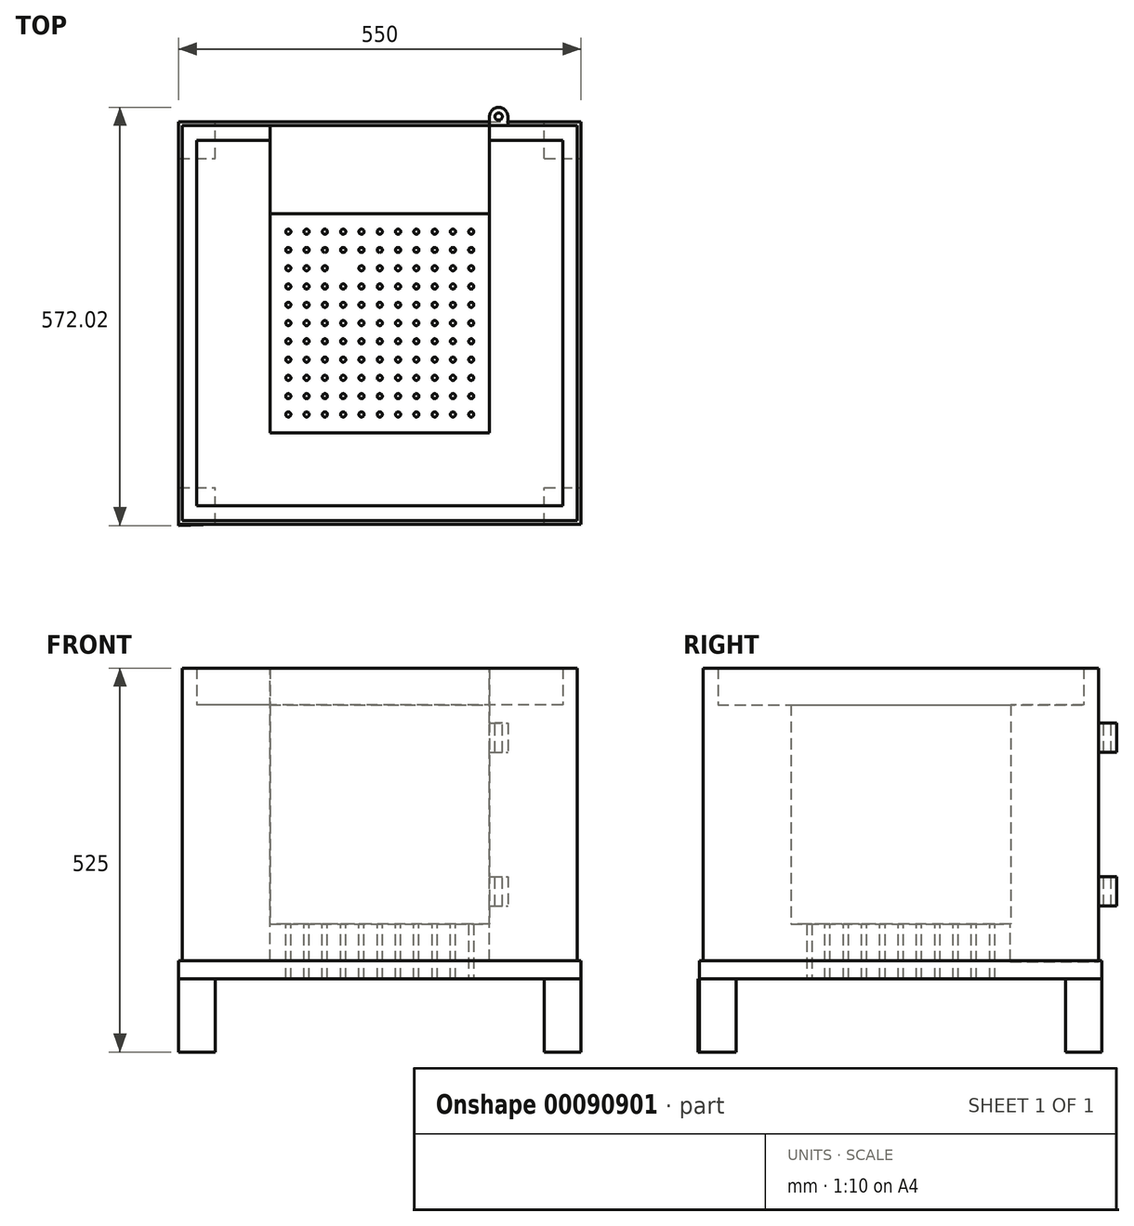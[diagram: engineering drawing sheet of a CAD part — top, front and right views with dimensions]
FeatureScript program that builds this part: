
annotation { "Feature Type Name" : "Feature", "Feature Type Description" : "" }
export const myFeature = defineFeature(function(context is Context, id is Id, definition is map)
    precondition{}
    {
        {
            var Q0;
            Q0=qCreatedBy(makeId("Top.planeOp"),FACE);
            var sketch = newSketch(context, id + "F0", { "sketchPlane" : qUnion([Q0])});
            skPoint(sketch, "E0.middle", {"position": v(0, 0) * mm});
            skLineSegment(sketch, "E1.bottom", {"start": v(225, 225) * mm, "end": v(275, 225) * mm});
            skLineSegment(sketch, "E1.top", {"start": v(225, 275) * mm, "end": v(275, 275) * mm});
            skLineSegment(sketch, "E1.left", {"start": v(225, 225) * mm, "end": v(225, 275) * mm});
            skLineSegment(sketch, "E1.right", {"start": v(275, 225) * mm, "end": v(275, 275) * mm});
            skLineSegment(sketch, "E2.top", {"start": v(225, -225) * mm, "end": v(275, -225) * mm});
            skLineSegment(sketch, "E2.left", {"start": v(225, -275) * mm, "end": v(225, -225) * mm});
            skLineSegment(sketch, "E2.right", {"start": v(275, -275) * mm, "end": v(275, -225) * mm});
            skLineSegment(sketch, "E3", {"start": v(225, -275) * mm, "end": v(275, -275) * mm});
            skLineSegment(sketch, "E4.top", {"start": v(-275, -225) * mm, "end": v(-225, -225) * mm});
            skLineSegment(sketch, "E4.left", {"start": v(-275, -277.02) * mm, "end": v(-275, -225) * mm});
            skLineSegment(sketch, "E4.right", {"start": v(-225, -275) * mm, "end": v(-225, -225) * mm});
            skLineSegment(sketch, "E5", {"start": v(-275, -277.02) * mm, "end": v(-225, -275) * mm});
            skLineSegment(sketch, "E6.top", {"start": v(-275, 275) * mm, "end": v(-225, 275) * mm});
            skLineSegment(sketch, "E6.left", {"start": v(-275, 225) * mm, "end": v(-275, 275) * mm});
            skLineSegment(sketch, "E6.right", {"start": v(-225, 225) * mm, "end": v(-225, 275) * mm});
            skLineSegment(sketch, "E7", {"start": v(-275, 225) * mm, "end": v(-225, 225) * mm});
            skSolve(sketch);
        }
        {
            var Q0;
            Q0=makeQuery(id+"F0.imprint","IMPRINT",FACE,{"disambiguationData":[TD([[makeQuery(id+"F0.imprint","IMPRINT",EDGE,{"derivedFrom":sQuery(id+"F0.wireOp",EDGE,"E1.bottom")}),1.0]])]});
            var Q1;
            Q1=makeQuery(id+"F0.imprint","IMPRINT",FACE,{"disambiguationData":[TD([[makeQuery(id+"F0.imprint","IMPRINT",EDGE,{"derivedFrom":sQuery(id+"F0.wireOp",EDGE,"E2.top")}),-1.0]])]});
            var Q2;
            Q2=makeQuery(id+"F0.imprint","IMPRINT",FACE,{"disambiguationData":[TD([[makeQuery(id+"F0.imprint","IMPRINT",EDGE,{"derivedFrom":sQuery(id+"F0.wireOp",EDGE,"E4.top")}),-1.0]])]});
            var Q3;
            Q3=makeQuery(id+"F0.imprint","IMPRINT",FACE,{"disambiguationData":[TD([[makeQuery(id+"F0.imprint","IMPRINT",EDGE,{"derivedFrom":sQuery(id+"F0.wireOp",EDGE,"E6.top")}),-1.0]])]});
            extrude(context, id + "F1", {"entities" : qUnion([Q0, Q1, Q2, Q3]), "depth" : 100 * mm});
        }
        {
            var Q0;
            Q0=makeQuery(id+"F1.opExtrude","CAP_FACE",FACE,{"disambiguationData":[OSD([sQuery(id+"F0.wireOp",EDGE,"E6.top"),sQuery(id+"F0.wireOp",EDGE,"E6.left"),sQuery(id+"F0.wireOp",EDGE,"E6.right"),sQuery(id+"F0.wireOp",EDGE,"E7")])],"isStart":false});
            var sketch = newSketch(context, id + "F2", { "sketchPlane" : qUnion([Q0])});
            skLineSegment(sketch, "E8.bottom", {"start": v(-275, 275) * mm, "end": v(275, 275) * mm});
            skLineSegment(sketch, "E8.top", {"start": v(-275, -275) * mm, "end": v(275, -275) * mm});
            skLineSegment(sketch, "E8.left", {"start": v(-275, 275) * mm, "end": v(-275, -275) * mm});
            skLineSegment(sketch, "E8.right", {"start": v(275, 275) * mm, "end": v(275, -275) * mm});
            skSolve(sketch);
        }
        {
            var Q0;
            Q0 = qSketchRegion(id + "F2", true);
            var Q1;
            {var subQ3=sQuery(id+"F2.wireOp",EDGE,"E8.top");Q1=makeQuery(id+"F2.imprint","IMPRINT",FACE,{"disambiguationData":[TD([[makeQuery(id+"F2.imprint","IMPRINT",EDGE,{"derivedFrom":subQ3}),1.0]])]});}
            extrude(context, id + "F3", {"entities" : qUnion([Q0, Q1]), "depth" : 25 * mm});
        }
        {
            var Q0;
            Q0=makeQuery(id+"F3.opExtrude","CAP_FACE",FACE,{"disambiguationData":[OSD([sQuery(id+"F2.wireOp",EDGE,"E8.bottom"),sQuery(id+"F2.wireOp",EDGE,"E8.top"),sQuery(id+"F2.wireOp",EDGE,"E8.left"),sQuery(id+"F2.wireOp",EDGE,"E8.right")])],"isStart":false});
            var sketch = newSketch(context, id + "F4", { "sketchPlane" : qUnion([Q0])});
            skLineSegment(sketch, "E9.bottom", {"start": v(250, -250) * mm, "end": v(-250, -250) * mm});
            skLineSegment(sketch, "E9.top", {"start": v(250, 250) * mm, "end": v(-250, 250) * mm});
            skLineSegment(sketch, "E9.left", {"start": v(250, -250) * mm, "end": v(250, 250) * mm});
            skLineSegment(sketch, "E9.right", {"start": v(-250, -250) * mm, "end": v(-250, 250) * mm});
            skLineSegment(sketch, "E10.0", {"start": v(150, 150) * mm, "end": v(-150, 150) * mm});
            skLineSegment(sketch, "E10.1", {"start": v(150, -150) * mm, "end": v(150, 150) * mm});
            skLineSegment(sketch, "E10.2", {"start": v(-150, -150) * mm, "end": v(150, -150) * mm});
            skLineSegment(sketch, "E10.3", {"start": v(-150, 150) * mm, "end": v(-150, -150) * mm});
            skLineSegment(sketch, "E11.0", {"start": v(270, 270) * mm, "end": v(-270, 270) * mm});
            skLineSegment(sketch, "E11.1", {"start": v(270, -270) * mm, "end": v(270, 270) * mm});
            skLineSegment(sketch, "E11.2", {"start": v(-270, -270) * mm, "end": v(270, -270) * mm});
            skLineSegment(sketch, "E11.3", {"start": v(-270, 270) * mm, "end": v(-270, -270) * mm});
            skLineSegment(sketch, "E12", {"start": v(-150, 150) * mm, "end": v(-150, 275) * mm});
            skLineSegment(sketch, "E13", {"start": v(150, 150) * mm, "end": v(150, 275) * mm});
            skLineSegment(sketch, "E14.direction2", {"start": v(125, -125) * mm, "end": v(125, -104.2) * mm, "construction": true});
            skCircle(sketch, "E15", {"center": v(125, -125) * mm, "radius": 3.5 * mm});
            skSolve(sketch);
        }
        {
            var Q0;
            Q0=makeQuery(id+"F4.imprint","IMPRINT",FACE,{"disambiguationData":[TD([[makeQuery(id+"F4.imprint","IMPRINT",EDGE,{"derivedFrom":sQuery(id+"F4.wireOp",EDGE,"E9.bottom")}),1.0]])]});
            var Q1;
            {var subQ0=sQuery(id+"F4.wireOp",EDGE,"E13");var subQ1=sQuery(id+"F4.wireOp",EDGE,"E9.top");var subQ2=makeQuery(id+"F4.imprint","INTERSECT",VERTEX,{"derivedFrom":[subQ1,subQ0]});Q1=makeQuery(id+"F4.imprint","IMPRINT",FACE,{"disambiguationData":[TD([[makeQuery(id+"F4.imprint","IMPRINT",EDGE,{"disambiguationData":[TD([[subQ2,-1.0]])],"derivedFrom":subQ1}),-1.0]])]});}
            extrude(context, id + "F5", {"entities" : qUnion([Q0, Q1]), "operationType" : NewBodyOperationType.ADD, "depth" : 400 * mm});
        }
        {
            var Q0;
            Q0=makeQuery(id+"F4.imprint","IMPRINT",FACE,{"disambiguationData":[TD([[makeQuery(id+"F4.imprint","IMPRINT",EDGE,{"derivedFrom":sQuery(id+"F4.wireOp",EDGE,"E10.0")}),1.0]])]});
            extrude(context, id + "F6", {"entities" : qUnion([Q0]), "operationType" : NewBodyOperationType.ADD, "depth" : 50 * mm});
        }
        {
            var Q0;
            Q0=makeQuery(id+"F4.imprint","IMPRINT",FACE,{"disambiguationData":[TD([[makeQuery(id+"F4.imprint","IMPRINT",EDGE,{"derivedFrom":sQuery(id+"F4.wireOp",EDGE,"E9.bottom")}),-1.0]])]});
            var Q1;
            {var subQ5=sQuery(id+"F4.wireOp",EDGE,"E10.0");Q1=makeQuery(id+"F4.imprint","IMPRINT",FACE,{"disambiguationData":[TD([[makeQuery(id+"F4.imprint","IMPRINT",EDGE,{"derivedFrom":subQ5}),-1.0]])]});}
            extrude(context, id + "F7", {"entities" : qUnion([Q0, Q1]), "operationType" : NewBodyOperationType.ADD, "depth" : 350 * mm});
        }
        {
            var Q0;
            Q0=makeQuery(id+"F6.opExtrude","CAP_FACE",FACE,{"disambiguationData":[OSD([sQuery(id+"F4.wireOp",EDGE,"E10.0"),sQuery(id+"F4.wireOp",EDGE,"E10.1"),sQuery(id+"F4.wireOp",EDGE,"E10.2"),sQuery(id+"F4.wireOp",EDGE,"E10.3"),sQuery(id+"F4.wireOp",EDGE,"E15")])],"isStart":false});
            var sketch = newSketch(context, id + "F8", { "sketchPlane" : qUnion([Q0])});
            skCircle(sketch, "E16", {"center": v(125, 125) * mm, "radius": 3.5 * mm});
            skCircle(sketch, "E17.0.1.0", {"center": v(125, 100) * mm, "radius": 3.5 * mm});
            skCircle(sketch, "E17.0.2.0", {"center": v(125, 75) * mm, "radius": 3.5 * mm});
            skCircle(sketch, "E17.0.3.0", {"center": v(125, 50) * mm, "radius": 3.5 * mm});
            skCircle(sketch, "E17.0.4.0", {"center": v(125, 25) * mm, "radius": 3.5 * mm});
            skCircle(sketch, "E17.0.5.0", {"center": v(125, 0) * mm, "radius": 3.5 * mm});
            skCircle(sketch, "E17.0.6.0", {"center": v(125, -25) * mm, "radius": 3.5 * mm});
            skCircle(sketch, "E17.0.7.0", {"center": v(125, -50) * mm, "radius": 3.5 * mm});
            skCircle(sketch, "E17.0.8.0", {"center": v(125, -75) * mm, "radius": 3.5 * mm});
            skCircle(sketch, "E17.0.9.0", {"center": v(125, -100) * mm, "radius": 3.5 * mm});
            skCircle(sketch, "E17.0.10.0", {"center": v(125, -125) * mm, "radius": 3.5 * mm});
            skCircle(sketch, "E17.1.0.0", {"center": v(100, 125) * mm, "radius": 3.5 * mm});
            skCircle(sketch, "E17.1.1.0", {"center": v(100, 100) * mm, "radius": 3.5 * mm});
            skCircle(sketch, "E17.1.2.0", {"center": v(100, 75) * mm, "radius": 3.5 * mm});
            skCircle(sketch, "E17.1.3.0", {"center": v(100, 50) * mm, "radius": 3.5 * mm});
            skCircle(sketch, "E17.1.4.0", {"center": v(100, 25) * mm, "radius": 3.5 * mm});
            skCircle(sketch, "E17.1.5.0", {"center": v(100, 0) * mm, "radius": 3.5 * mm});
            skCircle(sketch, "E17.1.6.0", {"center": v(100, -25) * mm, "radius": 3.5 * mm});
            skCircle(sketch, "E17.1.7.0", {"center": v(100, -50) * mm, "radius": 3.5 * mm});
            skCircle(sketch, "E17.1.8.0", {"center": v(100, -75) * mm, "radius": 3.5 * mm});
            skCircle(sketch, "E17.1.9.0", {"center": v(100, -100) * mm, "radius": 3.5 * mm});
            skCircle(sketch, "E17.1.10.0", {"center": v(100, -125) * mm, "radius": 3.5 * mm});
            skCircle(sketch, "E17.2.0.0", {"center": v(75, 125) * mm, "radius": 3.5 * mm});
            skCircle(sketch, "E17.2.1.0", {"center": v(75, 100) * mm, "radius": 3.5 * mm});
            skCircle(sketch, "E17.2.2.0", {"center": v(75, 75) * mm, "radius": 3.5 * mm});
            skCircle(sketch, "E17.2.3.0", {"center": v(75, 50) * mm, "radius": 3.5 * mm});
            skCircle(sketch, "E17.2.4.0", {"center": v(75, 25) * mm, "radius": 3.5 * mm});
            skCircle(sketch, "E17.2.5.0", {"center": v(75, 0) * mm, "radius": 3.5 * mm});
            skCircle(sketch, "E17.2.6.0", {"center": v(75, -25) * mm, "radius": 3.5 * mm});
            skCircle(sketch, "E17.2.7.0", {"center": v(75, -50) * mm, "radius": 3.5 * mm});
            skCircle(sketch, "E17.2.8.0", {"center": v(75, -75) * mm, "radius": 3.5 * mm});
            skCircle(sketch, "E17.2.9.0", {"center": v(75, -100) * mm, "radius": 3.5 * mm});
            skCircle(sketch, "E17.2.10.0", {"center": v(75, -125) * mm, "radius": 3.5 * mm});
            skCircle(sketch, "E17.3.0.0", {"center": v(50, 125) * mm, "radius": 3.5 * mm});
            skCircle(sketch, "E17.3.1.0", {"center": v(50, 100) * mm, "radius": 3.5 * mm});
            skCircle(sketch, "E17.3.2.0", {"center": v(50, 75) * mm, "radius": 3.5 * mm});
            skCircle(sketch, "E17.3.3.0", {"center": v(50, 50) * mm, "radius": 3.5 * mm});
            skCircle(sketch, "E17.3.4.0", {"center": v(50, 25) * mm, "radius": 3.5 * mm});
            skCircle(sketch, "E17.3.5.0", {"center": v(50, 0) * mm, "radius": 3.5 * mm});
            skCircle(sketch, "E17.3.6.0", {"center": v(50, -25) * mm, "radius": 3.5 * mm});
            skCircle(sketch, "E17.3.7.0", {"center": v(50, -50) * mm, "radius": 3.5 * mm});
            skCircle(sketch, "E17.3.8.0", {"center": v(50, -75) * mm, "radius": 3.5 * mm});
            skCircle(sketch, "E17.3.9.0", {"center": v(50, -100) * mm, "radius": 3.5 * mm});
            skCircle(sketch, "E17.3.10.0", {"center": v(50, -125) * mm, "radius": 3.5 * mm});
            skCircle(sketch, "E17.4.0.0", {"center": v(25, 125) * mm, "radius": 3.5 * mm});
            skCircle(sketch, "E17.4.1.0", {"center": v(25, 100) * mm, "radius": 3.5 * mm});
            skCircle(sketch, "E17.4.2.0", {"center": v(25, 75) * mm, "radius": 3.5 * mm});
            skCircle(sketch, "E17.4.3.0", {"center": v(25, 50) * mm, "radius": 3.5 * mm});
            skCircle(sketch, "E17.4.4.0", {"center": v(25, 25) * mm, "radius": 3.5 * mm});
            skCircle(sketch, "E17.4.5.0", {"center": v(25, 0) * mm, "radius": 3.5 * mm});
            skCircle(sketch, "E17.4.6.0", {"center": v(25, -25) * mm, "radius": 3.5 * mm});
            skCircle(sketch, "E17.4.7.0", {"center": v(25, -50) * mm, "radius": 3.5 * mm});
            skCircle(sketch, "E17.4.8.0", {"center": v(25, -75) * mm, "radius": 3.5 * mm});
            skCircle(sketch, "E17.4.9.0", {"center": v(25, -100) * mm, "radius": 3.5 * mm});
            skCircle(sketch, "E17.4.10.0", {"center": v(25, -125) * mm, "radius": 3.5 * mm});
            skCircle(sketch, "E17.5.0.0", {"center": v(0, 125) * mm, "radius": 3.5 * mm});
            skCircle(sketch, "E17.5.1.0", {"center": v(0, 100) * mm, "radius": 3.5 * mm});
            skCircle(sketch, "E17.5.2.0", {"center": v(0, 75) * mm, "radius": 3.5 * mm});
            skCircle(sketch, "E17.5.3.0", {"center": v(0, 50) * mm, "radius": 3.5 * mm});
            skCircle(sketch, "E17.5.4.0", {"center": v(0, 25) * mm, "radius": 3.5 * mm});
            skCircle(sketch, "E17.5.5.0", {"center": v(0, 0) * mm, "radius": 3.5 * mm});
            skCircle(sketch, "E17.5.6.0", {"center": v(0, -25) * mm, "radius": 3.5 * mm});
            skCircle(sketch, "E17.5.7.0", {"center": v(0, -50) * mm, "radius": 3.5 * mm});
            skCircle(sketch, "E17.5.8.0", {"center": v(0, -75) * mm, "radius": 3.5 * mm});
            skCircle(sketch, "E17.5.9.0", {"center": v(0, -100) * mm, "radius": 3.5 * mm});
            skCircle(sketch, "E17.5.10.0", {"center": v(0, -125) * mm, "radius": 3.5 * mm});
            skCircle(sketch, "E17.6.0.0", {"center": v(-25, 125) * mm, "radius": 3.5 * mm});
            skCircle(sketch, "E17.6.1.0", {"center": v(-25, 100) * mm, "radius": 3.5 * mm});
            skCircle(sketch, "E17.6.2.0", {"center": v(-25, 75) * mm, "radius": 3.5 * mm});
            skCircle(sketch, "E17.6.3.0", {"center": v(-25, 50) * mm, "radius": 3.5 * mm});
            skCircle(sketch, "E17.6.4.0", {"center": v(-25, 25) * mm, "radius": 3.5 * mm});
            skCircle(sketch, "E17.6.5.0", {"center": v(-25, 0) * mm, "radius": 3.5 * mm});
            skCircle(sketch, "E17.6.6.0", {"center": v(-25, -25) * mm, "radius": 3.5 * mm});
            skCircle(sketch, "E17.6.7.0", {"center": v(-25, -50) * mm, "radius": 3.5 * mm});
            skCircle(sketch, "E17.6.8.0", {"center": v(-25, -75) * mm, "radius": 3.5 * mm});
            skCircle(sketch, "E17.6.9.0", {"center": v(-25, -100) * mm, "radius": 3.5 * mm});
            skCircle(sketch, "E17.6.10.0", {"center": v(-25, -125) * mm, "radius": 3.5 * mm});
            skCircle(sketch, "E17.7.0.0", {"center": v(-50, 125) * mm, "radius": 3.5 * mm});
            skCircle(sketch, "E17.7.1.0", {"center": v(-50, 100) * mm, "radius": 3.5 * mm});
            skCircle(sketch, "E17.7.2.0", {"center": v(-50, 75) * mm, "radius": 3.5 * mm});
            skCircle(sketch, "E17.7.3.0", {"center": v(-50, 50) * mm, "radius": 3.5 * mm});
            skCircle(sketch, "E17.7.4.0", {"center": v(-50, 25) * mm, "radius": 3.5 * mm});
            skCircle(sketch, "E17.7.5.0", {"center": v(-50, 0) * mm, "radius": 3.5 * mm});
            skCircle(sketch, "E17.7.6.0", {"center": v(-50, -25) * mm, "radius": 3.5 * mm});
            skCircle(sketch, "E17.7.7.0", {"center": v(-50, -50) * mm, "radius": 3.5 * mm});
            skCircle(sketch, "E17.7.8.0", {"center": v(-50, -75) * mm, "radius": 3.5 * mm});
            skCircle(sketch, "E17.7.9.0", {"center": v(-50, -100) * mm, "radius": 3.5 * mm});
            skCircle(sketch, "E17.7.10.0", {"center": v(-50, -125) * mm, "radius": 3.5 * mm});
            skCircle(sketch, "E17.8.0.0", {"center": v(-75, 125) * mm, "radius": 3.5 * mm});
            skCircle(sketch, "E17.8.1.0", {"center": v(-75, 100) * mm, "radius": 3.5 * mm});
            skCircle(sketch, "E17.8.2.0", {"center": v(-75, 75) * mm, "radius": 3.5 * mm});
            skCircle(sketch, "E17.8.3.0", {"center": v(-75, 50) * mm, "radius": 3.5 * mm});
            skCircle(sketch, "E17.8.4.0", {"center": v(-75, 25) * mm, "radius": 3.5 * mm});
            skCircle(sketch, "E17.8.5.0", {"center": v(-75, 0) * mm, "radius": 3.5 * mm});
            skCircle(sketch, "E17.8.6.0", {"center": v(-75, -25) * mm, "radius": 3.5 * mm});
            skCircle(sketch, "E17.8.7.0", {"center": v(-75, -50) * mm, "radius": 3.5 * mm});
            skCircle(sketch, "E17.8.8.0", {"center": v(-75, -75) * mm, "radius": 3.5 * mm});
            skCircle(sketch, "E17.8.9.0", {"center": v(-75, -100) * mm, "radius": 3.5 * mm});
            skCircle(sketch, "E17.8.10.0", {"center": v(-75, -125) * mm, "radius": 3.5 * mm});
            skCircle(sketch, "E17.9.0.0", {"center": v(-100, 125) * mm, "radius": 3.5 * mm});
            skCircle(sketch, "E17.9.1.0", {"center": v(-100, 100) * mm, "radius": 3.5 * mm});
            skCircle(sketch, "E17.9.2.0", {"center": v(-100, 75) * mm, "radius": 3.5 * mm});
            skCircle(sketch, "E17.9.3.0", {"center": v(-100, 50) * mm, "radius": 3.5 * mm});
            skCircle(sketch, "E17.9.4.0", {"center": v(-100, 25) * mm, "radius": 3.5 * mm});
            skCircle(sketch, "E17.9.5.0", {"center": v(-100, 0) * mm, "radius": 3.5 * mm});
            skCircle(sketch, "E17.9.6.0", {"center": v(-100, -25) * mm, "radius": 3.5 * mm});
            skCircle(sketch, "E17.9.7.0", {"center": v(-100, -50) * mm, "radius": 3.5 * mm});
            skCircle(sketch, "E17.9.8.0", {"center": v(-100, -75) * mm, "radius": 3.5 * mm});
            skCircle(sketch, "E17.9.9.0", {"center": v(-100, -100) * mm, "radius": 3.5 * mm});
            skCircle(sketch, "E17.9.10.0", {"center": v(-100, -125) * mm, "radius": 3.5 * mm});
            skCircle(sketch, "E17.10.0.0", {"center": v(-125, 125) * mm, "radius": 3.5 * mm});
            skCircle(sketch, "E17.10.1.0", {"center": v(-125, 100) * mm, "radius": 3.5 * mm});
            skCircle(sketch, "E17.10.2.0", {"center": v(-125, 75) * mm, "radius": 3.5 * mm});
            skCircle(sketch, "E17.10.3.0", {"center": v(-125, 50) * mm, "radius": 3.5 * mm});
            skCircle(sketch, "E17.10.4.0", {"center": v(-125, 25) * mm, "radius": 3.5 * mm});
            skCircle(sketch, "E17.10.5.0", {"center": v(-125, 0) * mm, "radius": 3.5 * mm});
            skCircle(sketch, "E17.10.6.0", {"center": v(-125, -25) * mm, "radius": 3.5 * mm});
            skCircle(sketch, "E17.10.7.0", {"center": v(-125, -50) * mm, "radius": 3.5 * mm});
            skCircle(sketch, "E17.10.8.0", {"center": v(-125, -75) * mm, "radius": 3.5 * mm});
            skCircle(sketch, "E17.10.9.0", {"center": v(-125, -100) * mm, "radius": 3.5 * mm});
            skCircle(sketch, "E17.10.10.0", {"center": v(-125, -125) * mm, "radius": 3.5 * mm});
            skLineSegment(sketch, "E17.direction1", {"start": v(125, 125) * mm, "end": v(100, 125) * mm, "construction": true});
            skLineSegment(sketch, "E17.direction2", {"start": v(125, 125) * mm, "end": v(125, 100) * mm, "construction": true});
            skSolve(sketch);
        }
        {
            var Q0;
            Q0=makeQuery(id+"F8.imprint","IMPRINT",FACE,{"disambiguationData":[TD([[makeQuery(id+"F8.imprint","IMPRINT",EDGE,{"derivedFrom":sQuery(id+"F8.wireOp",EDGE,"E16")}),1.0]])]});
            var Q1;
            Q1=makeQuery(id+"F8.imprint","IMPRINT",FACE,{"disambiguationData":[TD([[makeQuery(id+"F8.imprint","IMPRINT",EDGE,{"derivedFrom":sQuery(id+"F8.wireOp",EDGE,"E17.0.1.0")}),1.0]])]});
            var Q2;
            Q2=makeQuery(id+"F8.imprint","IMPRINT",FACE,{"disambiguationData":[TD([[makeQuery(id+"F8.imprint","IMPRINT",EDGE,{"derivedFrom":sQuery(id+"F8.wireOp",EDGE,"E17.0.2.0")}),1.0]])]});
            var Q3;
            Q3=makeQuery(id+"F8.imprint","IMPRINT",FACE,{"disambiguationData":[TD([[makeQuery(id+"F8.imprint","IMPRINT",EDGE,{"derivedFrom":sQuery(id+"F8.wireOp",EDGE,"E17.0.3.0")}),1.0]])]});
            var Q4;
            Q4=makeQuery(id+"F8.imprint","IMPRINT",FACE,{"disambiguationData":[TD([[makeQuery(id+"F8.imprint","IMPRINT",EDGE,{"derivedFrom":sQuery(id+"F8.wireOp",EDGE,"E17.0.4.0")}),1.0]])]});
            var Q5;
            Q5=makeQuery(id+"F8.imprint","IMPRINT",FACE,{"disambiguationData":[TD([[makeQuery(id+"F8.imprint","IMPRINT",EDGE,{"derivedFrom":sQuery(id+"F8.wireOp",EDGE,"E17.0.5.0")}),1.0]])]});
            var Q6;
            Q6=makeQuery(id+"F8.imprint","IMPRINT",FACE,{"disambiguationData":[TD([[makeQuery(id+"F8.imprint","IMPRINT",EDGE,{"derivedFrom":sQuery(id+"F8.wireOp",EDGE,"E17.0.6.0")}),1.0]])]});
            var Q7;
            Q7=makeQuery(id+"F8.imprint","IMPRINT",FACE,{"disambiguationData":[TD([[makeQuery(id+"F8.imprint","IMPRINT",EDGE,{"derivedFrom":sQuery(id+"F8.wireOp",EDGE,"E17.0.7.0")}),1.0]])]});
            var Q8;
            Q8=makeQuery(id+"F8.imprint","IMPRINT",FACE,{"disambiguationData":[TD([[makeQuery(id+"F8.imprint","IMPRINT",EDGE,{"derivedFrom":sQuery(id+"F8.wireOp",EDGE,"E17.0.8.0")}),1.0]])]});
            var Q9;
            Q9=makeQuery(id+"F8.imprint","IMPRINT",FACE,{"disambiguationData":[TD([[makeQuery(id+"F8.imprint","IMPRINT",EDGE,{"derivedFrom":sQuery(id+"F8.wireOp",EDGE,"E17.0.9.0")}),1.0]])]});
            var Q10;
            Q10=makeQuery(id+"F8.imprint","IMPRINT",FACE,{"disambiguationData":[TD([[makeQuery(id+"F8.imprint","IMPRINT",EDGE,{"derivedFrom":sQuery(id+"F8.wireOp",EDGE,"E17.0.10.0")}),1.0]])]});
            var Q11;
            Q11=makeQuery(id+"F8.imprint","IMPRINT",FACE,{"disambiguationData":[TD([[makeQuery(id+"F8.imprint","IMPRINT",EDGE,{"derivedFrom":sQuery(id+"F8.wireOp",EDGE,"E17.1.0.0")}),1.0]])]});
            var Q12;
            Q12=makeQuery(id+"F8.imprint","IMPRINT",FACE,{"disambiguationData":[TD([[makeQuery(id+"F8.imprint","IMPRINT",EDGE,{"derivedFrom":sQuery(id+"F8.wireOp",EDGE,"E17.1.1.0")}),1.0]])]});
            var Q13;
            Q13=makeQuery(id+"F8.imprint","IMPRINT",FACE,{"disambiguationData":[TD([[makeQuery(id+"F8.imprint","IMPRINT",EDGE,{"derivedFrom":sQuery(id+"F8.wireOp",EDGE,"E17.1.2.0")}),1.0]])]});
            var Q14;
            Q14=makeQuery(id+"F8.imprint","IMPRINT",FACE,{"disambiguationData":[TD([[makeQuery(id+"F8.imprint","IMPRINT",EDGE,{"derivedFrom":sQuery(id+"F8.wireOp",EDGE,"E17.1.3.0")}),1.0]])]});
            var Q15;
            Q15=makeQuery(id+"F8.imprint","IMPRINT",FACE,{"disambiguationData":[TD([[makeQuery(id+"F8.imprint","IMPRINT",EDGE,{"derivedFrom":sQuery(id+"F8.wireOp",EDGE,"E17.1.4.0")}),1.0]])]});
            var Q16;
            Q16=makeQuery(id+"F8.imprint","IMPRINT",FACE,{"disambiguationData":[TD([[makeQuery(id+"F8.imprint","IMPRINT",EDGE,{"derivedFrom":sQuery(id+"F8.wireOp",EDGE,"E17.1.5.0")}),1.0]])]});
            var Q17;
            Q17=makeQuery(id+"F8.imprint","IMPRINT",FACE,{"disambiguationData":[TD([[makeQuery(id+"F8.imprint","IMPRINT",EDGE,{"derivedFrom":sQuery(id+"F8.wireOp",EDGE,"E17.1.6.0")}),1.0]])]});
            var Q18;
            Q18=makeQuery(id+"F8.imprint","IMPRINT",FACE,{"disambiguationData":[TD([[makeQuery(id+"F8.imprint","IMPRINT",EDGE,{"derivedFrom":sQuery(id+"F8.wireOp",EDGE,"E17.1.7.0")}),1.0]])]});
            var Q19;
            Q19=makeQuery(id+"F8.imprint","IMPRINT",FACE,{"disambiguationData":[TD([[makeQuery(id+"F8.imprint","IMPRINT",EDGE,{"derivedFrom":sQuery(id+"F8.wireOp",EDGE,"E17.1.8.0")}),1.0]])]});
            var Q20;
            Q20=makeQuery(id+"F8.imprint","IMPRINT",FACE,{"disambiguationData":[TD([[makeQuery(id+"F8.imprint","IMPRINT",EDGE,{"derivedFrom":sQuery(id+"F8.wireOp",EDGE,"E17.1.9.0")}),1.0]])]});
            var Q21;
            Q21=makeQuery(id+"F8.imprint","IMPRINT",FACE,{"disambiguationData":[TD([[makeQuery(id+"F8.imprint","IMPRINT",EDGE,{"derivedFrom":sQuery(id+"F8.wireOp",EDGE,"E17.1.10.0")}),1.0]])]});
            var Q22;
            Q22=makeQuery(id+"F8.imprint","IMPRINT",FACE,{"disambiguationData":[TD([[makeQuery(id+"F8.imprint","IMPRINT",EDGE,{"derivedFrom":sQuery(id+"F8.wireOp",EDGE,"E17.2.0.0")}),1.0]])]});
            var Q23;
            Q23=makeQuery(id+"F8.imprint","IMPRINT",FACE,{"disambiguationData":[TD([[makeQuery(id+"F8.imprint","IMPRINT",EDGE,{"derivedFrom":sQuery(id+"F8.wireOp",EDGE,"E17.2.1.0")}),1.0]])]});
            var Q24;
            Q24=makeQuery(id+"F8.imprint","IMPRINT",FACE,{"disambiguationData":[TD([[makeQuery(id+"F8.imprint","IMPRINT",EDGE,{"derivedFrom":sQuery(id+"F8.wireOp",EDGE,"E17.2.2.0")}),1.0]])]});
            var Q25;
            Q25=makeQuery(id+"F8.imprint","IMPRINT",FACE,{"disambiguationData":[TD([[makeQuery(id+"F8.imprint","IMPRINT",EDGE,{"derivedFrom":sQuery(id+"F8.wireOp",EDGE,"E17.2.3.0")}),1.0]])]});
            var Q26;
            Q26=makeQuery(id+"F8.imprint","IMPRINT",FACE,{"disambiguationData":[TD([[makeQuery(id+"F8.imprint","IMPRINT",EDGE,{"derivedFrom":sQuery(id+"F8.wireOp",EDGE,"E17.2.4.0")}),1.0]])]});
            var Q27;
            Q27=makeQuery(id+"F8.imprint","IMPRINT",FACE,{"disambiguationData":[TD([[makeQuery(id+"F8.imprint","IMPRINT",EDGE,{"derivedFrom":sQuery(id+"F8.wireOp",EDGE,"E17.2.5.0")}),1.0]])]});
            var Q28;
            Q28=makeQuery(id+"F8.imprint","IMPRINT",FACE,{"disambiguationData":[TD([[makeQuery(id+"F8.imprint","IMPRINT",EDGE,{"derivedFrom":sQuery(id+"F8.wireOp",EDGE,"E17.2.6.0")}),1.0]])]});
            var Q29;
            Q29=makeQuery(id+"F8.imprint","IMPRINT",FACE,{"disambiguationData":[TD([[makeQuery(id+"F8.imprint","IMPRINT",EDGE,{"derivedFrom":sQuery(id+"F8.wireOp",EDGE,"E17.2.7.0")}),1.0]])]});
            var Q30;
            Q30=makeQuery(id+"F8.imprint","IMPRINT",FACE,{"disambiguationData":[TD([[makeQuery(id+"F8.imprint","IMPRINT",EDGE,{"derivedFrom":sQuery(id+"F8.wireOp",EDGE,"E17.2.8.0")}),1.0]])]});
            var Q31;
            Q31=makeQuery(id+"F8.imprint","IMPRINT",FACE,{"disambiguationData":[TD([[makeQuery(id+"F8.imprint","IMPRINT",EDGE,{"derivedFrom":sQuery(id+"F8.wireOp",EDGE,"E17.2.9.0")}),1.0]])]});
            var Q32;
            Q32=makeQuery(id+"F8.imprint","IMPRINT",FACE,{"disambiguationData":[TD([[makeQuery(id+"F8.imprint","IMPRINT",EDGE,{"derivedFrom":sQuery(id+"F8.wireOp",EDGE,"E17.2.10.0")}),1.0]])]});
            var Q33;
            Q33=makeQuery(id+"F8.imprint","IMPRINT",FACE,{"disambiguationData":[TD([[makeQuery(id+"F8.imprint","IMPRINT",EDGE,{"derivedFrom":sQuery(id+"F8.wireOp",EDGE,"E17.3.0.0")}),1.0]])]});
            var Q34;
            Q34=makeQuery(id+"F8.imprint","IMPRINT",FACE,{"disambiguationData":[TD([[makeQuery(id+"F8.imprint","IMPRINT",EDGE,{"derivedFrom":sQuery(id+"F8.wireOp",EDGE,"E17.3.1.0")}),1.0]])]});
            var Q35;
            Q35=makeQuery(id+"F8.imprint","IMPRINT",FACE,{"disambiguationData":[TD([[makeQuery(id+"F8.imprint","IMPRINT",EDGE,{"derivedFrom":sQuery(id+"F8.wireOp",EDGE,"E17.3.2.0")}),1.0]])]});
            var Q36;
            Q36=makeQuery(id+"F8.imprint","IMPRINT",FACE,{"disambiguationData":[TD([[makeQuery(id+"F8.imprint","IMPRINT",EDGE,{"derivedFrom":sQuery(id+"F8.wireOp",EDGE,"E17.3.3.0")}),1.0]])]});
            var Q37;
            Q37=makeQuery(id+"F8.imprint","IMPRINT",FACE,{"disambiguationData":[TD([[makeQuery(id+"F8.imprint","IMPRINT",EDGE,{"derivedFrom":sQuery(id+"F8.wireOp",EDGE,"E17.3.4.0")}),1.0]])]});
            var Q38;
            Q38=makeQuery(id+"F8.imprint","IMPRINT",FACE,{"disambiguationData":[TD([[makeQuery(id+"F8.imprint","IMPRINT",EDGE,{"derivedFrom":sQuery(id+"F8.wireOp",EDGE,"E17.3.5.0")}),1.0]])]});
            var Q39;
            Q39=makeQuery(id+"F8.imprint","IMPRINT",FACE,{"disambiguationData":[TD([[makeQuery(id+"F8.imprint","IMPRINT",EDGE,{"derivedFrom":sQuery(id+"F8.wireOp",EDGE,"E17.3.6.0")}),1.0]])]});
            var Q40;
            Q40=makeQuery(id+"F8.imprint","IMPRINT",FACE,{"disambiguationData":[TD([[makeQuery(id+"F8.imprint","IMPRINT",EDGE,{"derivedFrom":sQuery(id+"F8.wireOp",EDGE,"E17.3.7.0")}),1.0]])]});
            var Q41;
            Q41=makeQuery(id+"F8.imprint","IMPRINT",FACE,{"disambiguationData":[TD([[makeQuery(id+"F8.imprint","IMPRINT",EDGE,{"derivedFrom":sQuery(id+"F8.wireOp",EDGE,"E17.3.8.0")}),1.0]])]});
            var Q42;
            Q42=makeQuery(id+"F8.imprint","IMPRINT",FACE,{"disambiguationData":[TD([[makeQuery(id+"F8.imprint","IMPRINT",EDGE,{"derivedFrom":sQuery(id+"F8.wireOp",EDGE,"E17.3.9.0")}),1.0]])]});
            var Q43;
            Q43=makeQuery(id+"F8.imprint","IMPRINT",FACE,{"disambiguationData":[TD([[makeQuery(id+"F8.imprint","IMPRINT",EDGE,{"derivedFrom":sQuery(id+"F8.wireOp",EDGE,"E17.3.10.0")}),1.0]])]});
            var Q44;
            Q44=makeQuery(id+"F8.imprint","IMPRINT",FACE,{"disambiguationData":[TD([[makeQuery(id+"F8.imprint","IMPRINT",EDGE,{"derivedFrom":sQuery(id+"F8.wireOp",EDGE,"E17.4.0.0")}),1.0]])]});
            var Q45;
            Q45=makeQuery(id+"F8.imprint","IMPRINT",FACE,{"disambiguationData":[TD([[makeQuery(id+"F8.imprint","IMPRINT",EDGE,{"derivedFrom":sQuery(id+"F8.wireOp",EDGE,"E17.4.1.0")}),1.0]])]});
            var Q46;
            Q46=makeQuery(id+"F8.imprint","IMPRINT",FACE,{"disambiguationData":[TD([[makeQuery(id+"F8.imprint","IMPRINT",EDGE,{"derivedFrom":sQuery(id+"F8.wireOp",EDGE,"E17.4.2.0")}),1.0]])]});
            var Q47;
            Q47=makeQuery(id+"F8.imprint","IMPRINT",FACE,{"disambiguationData":[TD([[makeQuery(id+"F8.imprint","IMPRINT",EDGE,{"derivedFrom":sQuery(id+"F8.wireOp",EDGE,"E17.4.3.0")}),1.0]])]});
            var Q48;
            Q48=makeQuery(id+"F8.imprint","IMPRINT",FACE,{"disambiguationData":[TD([[makeQuery(id+"F8.imprint","IMPRINT",EDGE,{"derivedFrom":sQuery(id+"F8.wireOp",EDGE,"E17.4.4.0")}),1.0]])]});
            var Q49;
            Q49=makeQuery(id+"F8.imprint","IMPRINT",FACE,{"disambiguationData":[TD([[makeQuery(id+"F8.imprint","IMPRINT",EDGE,{"derivedFrom":sQuery(id+"F8.wireOp",EDGE,"E17.4.5.0")}),1.0]])]});
            var Q50;
            Q50=makeQuery(id+"F8.imprint","IMPRINT",FACE,{"disambiguationData":[TD([[makeQuery(id+"F8.imprint","IMPRINT",EDGE,{"derivedFrom":sQuery(id+"F8.wireOp",EDGE,"E17.4.6.0")}),1.0]])]});
            var Q51;
            Q51=makeQuery(id+"F8.imprint","IMPRINT",FACE,{"disambiguationData":[TD([[makeQuery(id+"F8.imprint","IMPRINT",EDGE,{"derivedFrom":sQuery(id+"F8.wireOp",EDGE,"E17.4.7.0")}),1.0]])]});
            var Q52;
            Q52=makeQuery(id+"F8.imprint","IMPRINT",FACE,{"disambiguationData":[TD([[makeQuery(id+"F8.imprint","IMPRINT",EDGE,{"derivedFrom":sQuery(id+"F8.wireOp",EDGE,"E17.4.8.0")}),1.0]])]});
            var Q53;
            Q53=makeQuery(id+"F8.imprint","IMPRINT",FACE,{"disambiguationData":[TD([[makeQuery(id+"F8.imprint","IMPRINT",EDGE,{"derivedFrom":sQuery(id+"F8.wireOp",EDGE,"E17.4.9.0")}),1.0]])]});
            var Q54;
            Q54=makeQuery(id+"F8.imprint","IMPRINT",FACE,{"disambiguationData":[TD([[makeQuery(id+"F8.imprint","IMPRINT",EDGE,{"derivedFrom":sQuery(id+"F8.wireOp",EDGE,"E17.4.10.0")}),1.0]])]});
            var Q55;
            Q55=makeQuery(id+"F8.imprint","IMPRINT",FACE,{"disambiguationData":[TD([[makeQuery(id+"F8.imprint","IMPRINT",EDGE,{"derivedFrom":sQuery(id+"F8.wireOp",EDGE,"E17.5.0.0")}),1.0]])]});
            var Q56;
            Q56=makeQuery(id+"F8.imprint","IMPRINT",FACE,{"disambiguationData":[TD([[makeQuery(id+"F8.imprint","IMPRINT",EDGE,{"derivedFrom":sQuery(id+"F8.wireOp",EDGE,"E17.5.1.0")}),1.0]])]});
            var Q57;
            Q57=makeQuery(id+"F8.imprint","IMPRINT",FACE,{"disambiguationData":[TD([[makeQuery(id+"F8.imprint","IMPRINT",EDGE,{"derivedFrom":sQuery(id+"F8.wireOp",EDGE,"E17.5.2.0")}),1.0]])]});
            var Q58;
            Q58=makeQuery(id+"F8.imprint","IMPRINT",FACE,{"disambiguationData":[TD([[makeQuery(id+"F8.imprint","IMPRINT",EDGE,{"derivedFrom":sQuery(id+"F8.wireOp",EDGE,"E17.5.3.0")}),1.0]])]});
            var Q59;
            Q59=makeQuery(id+"F8.imprint","IMPRINT",FACE,{"disambiguationData":[TD([[makeQuery(id+"F8.imprint","IMPRINT",EDGE,{"derivedFrom":sQuery(id+"F8.wireOp",EDGE,"E17.5.4.0")}),1.0]])]});
            var Q60;
            Q60=makeQuery(id+"F8.imprint","IMPRINT",FACE,{"disambiguationData":[TD([[makeQuery(id+"F8.imprint","IMPRINT",EDGE,{"derivedFrom":sQuery(id+"F8.wireOp",EDGE,"E17.5.5.0")}),1.0]])]});
            var Q61;
            Q61=makeQuery(id+"F8.imprint","IMPRINT",FACE,{"disambiguationData":[TD([[makeQuery(id+"F8.imprint","IMPRINT",EDGE,{"derivedFrom":sQuery(id+"F8.wireOp",EDGE,"E17.5.6.0")}),1.0]])]});
            var Q62;
            Q62=makeQuery(id+"F8.imprint","IMPRINT",FACE,{"disambiguationData":[TD([[makeQuery(id+"F8.imprint","IMPRINT",EDGE,{"derivedFrom":sQuery(id+"F8.wireOp",EDGE,"E17.5.7.0")}),1.0]])]});
            var Q63;
            Q63=makeQuery(id+"F8.imprint","IMPRINT",FACE,{"disambiguationData":[TD([[makeQuery(id+"F8.imprint","IMPRINT",EDGE,{"derivedFrom":sQuery(id+"F8.wireOp",EDGE,"E17.5.8.0")}),1.0]])]});
            var Q64;
            Q64=makeQuery(id+"F8.imprint","IMPRINT",FACE,{"disambiguationData":[TD([[makeQuery(id+"F8.imprint","IMPRINT",EDGE,{"derivedFrom":sQuery(id+"F8.wireOp",EDGE,"E17.5.9.0")}),1.0]])]});
            var Q65;
            Q65=makeQuery(id+"F8.imprint","IMPRINT",FACE,{"disambiguationData":[TD([[makeQuery(id+"F8.imprint","IMPRINT",EDGE,{"derivedFrom":sQuery(id+"F8.wireOp",EDGE,"E17.5.10.0")}),1.0]])]});
            var Q66;
            Q66=makeQuery(id+"F8.imprint","IMPRINT",FACE,{"disambiguationData":[TD([[makeQuery(id+"F8.imprint","IMPRINT",EDGE,{"derivedFrom":sQuery(id+"F8.wireOp",EDGE,"E17.6.0.0")}),1.0]])]});
            var Q67;
            Q67=makeQuery(id+"F8.imprint","IMPRINT",FACE,{"disambiguationData":[TD([[makeQuery(id+"F8.imprint","IMPRINT",EDGE,{"derivedFrom":sQuery(id+"F8.wireOp",EDGE,"E17.6.1.0")}),1.0]])]});
            var Q68;
            Q68=makeQuery(id+"F8.imprint","IMPRINT",FACE,{"disambiguationData":[TD([[makeQuery(id+"F8.imprint","IMPRINT",EDGE,{"derivedFrom":sQuery(id+"F8.wireOp",EDGE,"E17.6.2.0")}),1.0]])]});
            var Q69;
            Q69=makeQuery(id+"F8.imprint","IMPRINT",FACE,{"disambiguationData":[TD([[makeQuery(id+"F8.imprint","IMPRINT",EDGE,{"derivedFrom":sQuery(id+"F8.wireOp",EDGE,"E17.6.3.0")}),1.0]])]});
            var Q70;
            Q70=makeQuery(id+"F8.imprint","IMPRINT",FACE,{"disambiguationData":[TD([[makeQuery(id+"F8.imprint","IMPRINT",EDGE,{"derivedFrom":sQuery(id+"F8.wireOp",EDGE,"E17.6.4.0")}),1.0]])]});
            var Q71;
            Q71=makeQuery(id+"F8.imprint","IMPRINT",FACE,{"disambiguationData":[TD([[makeQuery(id+"F8.imprint","IMPRINT",EDGE,{"derivedFrom":sQuery(id+"F8.wireOp",EDGE,"E17.6.5.0")}),1.0]])]});
            var Q72;
            Q72=makeQuery(id+"F8.imprint","IMPRINT",FACE,{"disambiguationData":[TD([[makeQuery(id+"F8.imprint","IMPRINT",EDGE,{"derivedFrom":sQuery(id+"F8.wireOp",EDGE,"E17.6.6.0")}),1.0]])]});
            var Q73;
            Q73=makeQuery(id+"F8.imprint","IMPRINT",FACE,{"disambiguationData":[TD([[makeQuery(id+"F8.imprint","IMPRINT",EDGE,{"derivedFrom":sQuery(id+"F8.wireOp",EDGE,"E17.6.7.0")}),1.0]])]});
            var Q74;
            Q74=makeQuery(id+"F8.imprint","IMPRINT",FACE,{"disambiguationData":[TD([[makeQuery(id+"F8.imprint","IMPRINT",EDGE,{"derivedFrom":sQuery(id+"F8.wireOp",EDGE,"E17.6.8.0")}),1.0]])]});
            var Q75;
            Q75=makeQuery(id+"F8.imprint","IMPRINT",FACE,{"disambiguationData":[TD([[makeQuery(id+"F8.imprint","IMPRINT",EDGE,{"derivedFrom":sQuery(id+"F8.wireOp",EDGE,"E17.6.9.0")}),1.0]])]});
            var Q76;
            Q76=makeQuery(id+"F8.imprint","IMPRINT",FACE,{"disambiguationData":[TD([[makeQuery(id+"F8.imprint","IMPRINT",EDGE,{"derivedFrom":sQuery(id+"F8.wireOp",EDGE,"E17.6.10.0")}),1.0]])]});
            var Q77;
            Q77=makeQuery(id+"F8.imprint","IMPRINT",FACE,{"disambiguationData":[TD([[makeQuery(id+"F8.imprint","IMPRINT",EDGE,{"derivedFrom":sQuery(id+"F8.wireOp",EDGE,"E17.7.0.0")}),1.0]])]});
            var Q78;
            Q78=makeQuery(id+"F8.imprint","IMPRINT",FACE,{"disambiguationData":[TD([[makeQuery(id+"F8.imprint","IMPRINT",EDGE,{"derivedFrom":sQuery(id+"F8.wireOp",EDGE,"E17.7.1.0")}),1.0]])]});
            var Q79;
            Q79=makeQuery(id+"F8.imprint","IMPRINT",FACE,{"disambiguationData":[TD([[makeQuery(id+"F8.imprint","IMPRINT",EDGE,{"derivedFrom":sQuery(id+"F8.wireOp",EDGE,"E17.7.3.0")}),1.0]])]});
            var Q80;
            Q80=makeQuery(id+"F8.imprint","IMPRINT",FACE,{"disambiguationData":[TD([[makeQuery(id+"F8.imprint","IMPRINT",EDGE,{"derivedFrom":sQuery(id+"F8.wireOp",EDGE,"E17.7.4.0")}),1.0]])]});
            var Q81;
            Q81=makeQuery(id+"F8.imprint","IMPRINT",FACE,{"disambiguationData":[TD([[makeQuery(id+"F8.imprint","IMPRINT",EDGE,{"derivedFrom":sQuery(id+"F8.wireOp",EDGE,"E17.7.5.0")}),1.0]])]});
            var Q82;
            Q82=makeQuery(id+"F8.imprint","IMPRINT",FACE,{"disambiguationData":[TD([[makeQuery(id+"F8.imprint","IMPRINT",EDGE,{"derivedFrom":sQuery(id+"F8.wireOp",EDGE,"E17.7.6.0")}),1.0]])]});
            var Q83;
            Q83=makeQuery(id+"F8.imprint","IMPRINT",FACE,{"disambiguationData":[TD([[makeQuery(id+"F8.imprint","IMPRINT",EDGE,{"derivedFrom":sQuery(id+"F8.wireOp",EDGE,"E17.7.7.0")}),1.0]])]});
            var Q84;
            Q84=makeQuery(id+"F8.imprint","IMPRINT",FACE,{"disambiguationData":[TD([[makeQuery(id+"F8.imprint","IMPRINT",EDGE,{"derivedFrom":sQuery(id+"F8.wireOp",EDGE,"E17.7.8.0")}),1.0]])]});
            var Q85;
            Q85=makeQuery(id+"F8.imprint","IMPRINT",FACE,{"disambiguationData":[TD([[makeQuery(id+"F8.imprint","IMPRINT",EDGE,{"derivedFrom":sQuery(id+"F8.wireOp",EDGE,"E17.7.9.0")}),1.0]])]});
            var Q86;
            Q86=makeQuery(id+"F8.imprint","IMPRINT",FACE,{"disambiguationData":[TD([[makeQuery(id+"F8.imprint","IMPRINT",EDGE,{"derivedFrom":sQuery(id+"F8.wireOp",EDGE,"E17.7.10.0")}),1.0]])]});
            var Q87;
            Q87=makeQuery(id+"F8.imprint","IMPRINT",FACE,{"disambiguationData":[TD([[makeQuery(id+"F8.imprint","IMPRINT",EDGE,{"derivedFrom":sQuery(id+"F8.wireOp",EDGE,"E17.8.0.0")}),1.0]])]});
            var Q88;
            Q88=makeQuery(id+"F8.imprint","IMPRINT",FACE,{"disambiguationData":[TD([[makeQuery(id+"F8.imprint","IMPRINT",EDGE,{"derivedFrom":sQuery(id+"F8.wireOp",EDGE,"E17.8.1.0")}),1.0]])]});
            var Q89;
            Q89=makeQuery(id+"F8.imprint","IMPRINT",FACE,{"disambiguationData":[TD([[makeQuery(id+"F8.imprint","IMPRINT",EDGE,{"derivedFrom":sQuery(id+"F8.wireOp",EDGE,"E17.8.2.0")}),1.0]])]});
            var Q90;
            Q90=makeQuery(id+"F8.imprint","IMPRINT",FACE,{"disambiguationData":[TD([[makeQuery(id+"F8.imprint","IMPRINT",EDGE,{"derivedFrom":sQuery(id+"F8.wireOp",EDGE,"E17.8.3.0")}),1.0]])]});
            var Q91;
            Q91=makeQuery(id+"F8.imprint","IMPRINT",FACE,{"disambiguationData":[TD([[makeQuery(id+"F8.imprint","IMPRINT",EDGE,{"derivedFrom":sQuery(id+"F8.wireOp",EDGE,"E17.8.4.0")}),1.0]])]});
            var Q92;
            Q92=makeQuery(id+"F8.imprint","IMPRINT",FACE,{"disambiguationData":[TD([[makeQuery(id+"F8.imprint","IMPRINT",EDGE,{"derivedFrom":sQuery(id+"F8.wireOp",EDGE,"E17.8.5.0")}),1.0]])]});
            var Q93;
            Q93=makeQuery(id+"F8.imprint","IMPRINT",FACE,{"disambiguationData":[TD([[makeQuery(id+"F8.imprint","IMPRINT",EDGE,{"derivedFrom":sQuery(id+"F8.wireOp",EDGE,"E17.8.6.0")}),1.0]])]});
            var Q94;
            Q94=makeQuery(id+"F8.imprint","IMPRINT",FACE,{"disambiguationData":[TD([[makeQuery(id+"F8.imprint","IMPRINT",EDGE,{"derivedFrom":sQuery(id+"F8.wireOp",EDGE,"E17.8.7.0")}),1.0]])]});
            var Q95;
            Q95=makeQuery(id+"F8.imprint","IMPRINT",FACE,{"disambiguationData":[TD([[makeQuery(id+"F8.imprint","IMPRINT",EDGE,{"derivedFrom":sQuery(id+"F8.wireOp",EDGE,"E17.8.8.0")}),1.0]])]});
            var Q96;
            Q96=makeQuery(id+"F8.imprint","IMPRINT",FACE,{"disambiguationData":[TD([[makeQuery(id+"F8.imprint","IMPRINT",EDGE,{"derivedFrom":sQuery(id+"F8.wireOp",EDGE,"E17.8.9.0")}),1.0]])]});
            var Q97;
            Q97=makeQuery(id+"F8.imprint","IMPRINT",FACE,{"disambiguationData":[TD([[makeQuery(id+"F8.imprint","IMPRINT",EDGE,{"derivedFrom":sQuery(id+"F8.wireOp",EDGE,"E17.8.10.0")}),1.0]])]});
            var Q98;
            Q98=makeQuery(id+"F8.imprint","IMPRINT",FACE,{"disambiguationData":[TD([[makeQuery(id+"F8.imprint","IMPRINT",EDGE,{"derivedFrom":sQuery(id+"F8.wireOp",EDGE,"E17.9.0.0")}),1.0]])]});
            var Q99;
            Q99=makeQuery(id+"F8.imprint","IMPRINT",FACE,{"disambiguationData":[TD([[makeQuery(id+"F8.imprint","IMPRINT",EDGE,{"derivedFrom":sQuery(id+"F8.wireOp",EDGE,"E17.9.1.0")}),1.0]])]});
            var Q100;
            Q100=makeQuery(id+"F8.imprint","IMPRINT",FACE,{"disambiguationData":[TD([[makeQuery(id+"F8.imprint","IMPRINT",EDGE,{"derivedFrom":sQuery(id+"F8.wireOp",EDGE,"E17.9.2.0")}),1.0]])]});
            var Q101;
            Q101=makeQuery(id+"F8.imprint","IMPRINT",FACE,{"disambiguationData":[TD([[makeQuery(id+"F8.imprint","IMPRINT",EDGE,{"derivedFrom":sQuery(id+"F8.wireOp",EDGE,"E17.9.3.0")}),1.0]])]});
            var Q102;
            Q102=makeQuery(id+"F8.imprint","IMPRINT",FACE,{"disambiguationData":[TD([[makeQuery(id+"F8.imprint","IMPRINT",EDGE,{"derivedFrom":sQuery(id+"F8.wireOp",EDGE,"E17.9.4.0")}),1.0]])]});
            var Q103;
            Q103=makeQuery(id+"F8.imprint","IMPRINT",FACE,{"disambiguationData":[TD([[makeQuery(id+"F8.imprint","IMPRINT",EDGE,{"derivedFrom":sQuery(id+"F8.wireOp",EDGE,"E17.9.5.0")}),1.0]])]});
            var Q104;
            Q104=makeQuery(id+"F8.imprint","IMPRINT",FACE,{"disambiguationData":[TD([[makeQuery(id+"F8.imprint","IMPRINT",EDGE,{"derivedFrom":sQuery(id+"F8.wireOp",EDGE,"E17.9.6.0")}),1.0]])]});
            var Q105;
            Q105=makeQuery(id+"F8.imprint","IMPRINT",FACE,{"disambiguationData":[TD([[makeQuery(id+"F8.imprint","IMPRINT",EDGE,{"derivedFrom":sQuery(id+"F8.wireOp",EDGE,"E17.9.7.0")}),1.0]])]});
            var Q106;
            Q106=makeQuery(id+"F8.imprint","IMPRINT",FACE,{"disambiguationData":[TD([[makeQuery(id+"F8.imprint","IMPRINT",EDGE,{"derivedFrom":sQuery(id+"F8.wireOp",EDGE,"E17.9.8.0")}),1.0]])]});
            var Q107;
            Q107=makeQuery(id+"F8.imprint","IMPRINT",FACE,{"disambiguationData":[TD([[makeQuery(id+"F8.imprint","IMPRINT",EDGE,{"derivedFrom":sQuery(id+"F8.wireOp",EDGE,"E17.9.9.0")}),1.0]])]});
            var Q108;
            Q108=makeQuery(id+"F8.imprint","IMPRINT",FACE,{"disambiguationData":[TD([[makeQuery(id+"F8.imprint","IMPRINT",EDGE,{"derivedFrom":sQuery(id+"F8.wireOp",EDGE,"E17.9.10.0")}),1.0]])]});
            var Q109;
            Q109=makeQuery(id+"F8.imprint","IMPRINT",FACE,{"disambiguationData":[TD([[makeQuery(id+"F8.imprint","IMPRINT",EDGE,{"derivedFrom":sQuery(id+"F8.wireOp",EDGE,"E17.10.0.0")}),1.0]])]});
            var Q110;
            Q110=makeQuery(id+"F8.imprint","IMPRINT",FACE,{"disambiguationData":[TD([[makeQuery(id+"F8.imprint","IMPRINT",EDGE,{"derivedFrom":sQuery(id+"F8.wireOp",EDGE,"E17.10.1.0")}),1.0]])]});
            var Q111;
            Q111=makeQuery(id+"F8.imprint","IMPRINT",FACE,{"disambiguationData":[TD([[makeQuery(id+"F8.imprint","IMPRINT",EDGE,{"derivedFrom":sQuery(id+"F8.wireOp",EDGE,"E17.10.2.0")}),1.0]])]});
            var Q112;
            Q112=makeQuery(id+"F8.imprint","IMPRINT",FACE,{"disambiguationData":[TD([[makeQuery(id+"F8.imprint","IMPRINT",EDGE,{"derivedFrom":sQuery(id+"F8.wireOp",EDGE,"E17.10.3.0")}),1.0]])]});
            var Q113;
            Q113=makeQuery(id+"F8.imprint","IMPRINT",FACE,{"disambiguationData":[TD([[makeQuery(id+"F8.imprint","IMPRINT",EDGE,{"derivedFrom":sQuery(id+"F8.wireOp",EDGE,"E17.10.4.0")}),1.0]])]});
            var Q114;
            Q114=makeQuery(id+"F8.imprint","IMPRINT",FACE,{"disambiguationData":[TD([[makeQuery(id+"F8.imprint","IMPRINT",EDGE,{"derivedFrom":sQuery(id+"F8.wireOp",EDGE,"E17.10.5.0")}),1.0]])]});
            var Q115;
            Q115=makeQuery(id+"F8.imprint","IMPRINT",FACE,{"disambiguationData":[TD([[makeQuery(id+"F8.imprint","IMPRINT",EDGE,{"derivedFrom":sQuery(id+"F8.wireOp",EDGE,"E17.10.6.0")}),1.0]])]});
            var Q116;
            Q116=makeQuery(id+"F8.imprint","IMPRINT",FACE,{"disambiguationData":[TD([[makeQuery(id+"F8.imprint","IMPRINT",EDGE,{"derivedFrom":sQuery(id+"F8.wireOp",EDGE,"E17.10.7.0")}),1.0]])]});
            var Q117;
            Q117=makeQuery(id+"F8.imprint","IMPRINT",FACE,{"disambiguationData":[TD([[makeQuery(id+"F8.imprint","IMPRINT",EDGE,{"derivedFrom":sQuery(id+"F8.wireOp",EDGE,"E17.10.8.0")}),1.0]])]});
            var Q118;
            Q118=makeQuery(id+"F8.imprint","IMPRINT",FACE,{"disambiguationData":[TD([[makeQuery(id+"F8.imprint","IMPRINT",EDGE,{"derivedFrom":sQuery(id+"F8.wireOp",EDGE,"E17.10.9.0")}),1.0]])]});
            var Q119;
            Q119=makeQuery(id+"F8.imprint","IMPRINT",FACE,{"disambiguationData":[TD([[makeQuery(id+"F8.imprint","IMPRINT",EDGE,{"derivedFrom":sQuery(id+"F8.wireOp",EDGE,"E17.10.10.0")}),1.0]])]});
            extrude(context, id + "F9", {"entities" : qUnion([Q0, Q1, Q2, Q3, Q4, Q5, Q6, Q7, Q8, Q9, Q10, Q11, Q12, Q13, Q14, Q15, Q16, Q17, Q18, Q19, Q20, Q21, Q22, Q23, Q24, Q25, Q26, Q27, Q28, Q29, Q30, Q31, Q32, Q33, Q34, Q35, Q36, Q37, Q38, Q39, Q40, Q41, Q42, Q43, Q44, Q45, Q46, Q47, Q48, Q49, Q50, Q51, Q52, Q53, Q54, Q55, Q56, Q57, Q58, Q59, Q60, Q61, Q62, Q63, Q64, Q65, Q66, Q67, Q68, Q69, Q70, Q71, Q72, Q73, Q74, Q75, Q76, Q77, Q78, Q79, Q80, Q81, Q82, Q83, Q84, Q85, Q86, Q87, Q88, Q89, Q90, Q91, Q92, Q93, Q94, Q95, Q96, Q97, Q98, Q99, Q100, Q101, Q102, Q103, Q104, Q105, Q106, Q107, Q108, Q109, Q110, Q111, Q112, Q113, Q114, Q115, Q116, Q117, Q118, Q119]), "operationType" : NewBodyOperationType.REMOVE, "oppositeDirection" : true, "depth" : 157.44 * mm});
        }
        {
            var Q0;
            Q0=makeQuery(id+"F5.opExtrude","SWEPT_FACE",FACE,{"disambiguationData":[OSD([sQuery(id+"F4.wireOp",EDGE,"E11.0")])]});
            var sketch = newSketch(context, id + "F10", { "sketchPlane" : qUnion([Q0])});
            skLineSegment(sketch, "E18", {"start": v(-150, 123.89) * mm, "end": v(-150, 532.55) * mm});
            skLineSegment(sketch, "E19", {"start": v(149.92, 125) * mm, "end": v(149.92, 525) * mm});
            skLineSegment(sketch, "E20", {"start": v(149.92, 525) * mm, "end": v(-150, 525) * mm});
            skLineSegment(sketch, "E21", {"start": v(-150, 123.89) * mm, "end": v(149.92, 125) * mm});
            skSolve(sketch);
        }
        {
            var Q0;
            Q0 = qSketchRegion(id + "F10", true);
            var Q1;
            {var subQ5=sQuery(id+"F10.wireOp",EDGE,"E19");Q1=makeQuery(id+"F10.imprint","IMPRINT",FACE,{"disambiguationData":[TD([[makeQuery(id+"F10.imprint","IMPRINT",EDGE,{"derivedFrom":subQ5}),1.0]])]});}
            extrude(context, id + "F11", {"entities" : qUnion([Q0, Q1]), "operationType" : NewBodyOperationType.REMOVE, "oppositeDirection" : true, "depth" : 120.33 * mm});
        }
        {
            var Q0;
            {var subQ0=sQuery(id+"F4.wireOp",EDGE,"E11.1");var subQ2=sQuery(id+"F4.wireOp",EDGE,"E11.0");Q0=makeQuery(id+"F11.boolean.opBoolean","SPLIT",FACE,{"disambiguationData":[TD([makeQuery(id+"F5.opExtrude","SWEPT_FACE",FACE,{"disambiguationData":[OSD([subQ0])]})])],"derivedFrom":makeQuery(id+"F5.opExtrude","SWEPT_FACE",FACE,{"disambiguationData":[OSD([subQ2])]})});}
            var sketch = newSketch(context, id + "F12", { "sketchPlane" : qUnion([Q0])});
            skLineSegment(sketch, "E22.bottom", {"start": v(-150, 450) * mm, "end": v(-175, 450) * mm});
            skLineSegment(sketch, "E22.top", {"start": v(-150, 410) * mm, "end": v(-175, 410) * mm});
            skLineSegment(sketch, "E22.left", {"start": v(-150, 450) * mm, "end": v(-150, 410) * mm});
            skLineSegment(sketch, "E22.right", {"start": v(-175, 450) * mm, "end": v(-175, 410) * mm});
            skPoint(sketch, "E23.oppositeSnap0", {"position": v(-162.5, 450) * mm});
            skLineSegment(sketch, "E23.bottom", {"start": v(-162.5, 450) * mm, "end": v(-162.5, 450) * mm});
            skLineSegment(sketch, "E23.top", {"start": v(-162.5, 525) * mm, "end": v(-162.5, 525) * mm});
            skLineSegment(sketch, "E23.left", {"start": v(-162.5, 450) * mm, "end": v(-162.5, 525) * mm});
            skLineSegment(sketch, "E23.right", {"start": v(-162.5, 450) * mm, "end": v(-162.5, 525) * mm});
            skLineSegment(sketch, "E24.bottom", {"start": v(-150, 240) * mm, "end": v(-175, 240) * mm});
            skLineSegment(sketch, "E24.top", {"start": v(-150, 200) * mm, "end": v(-175, 200) * mm});
            skLineSegment(sketch, "E24.left", {"start": v(-150, 240) * mm, "end": v(-150, 200) * mm});
            skLineSegment(sketch, "E24.right", {"start": v(-175, 240) * mm, "end": v(-175, 200) * mm});
            skSolve(sketch);
        }
        {
            var Q0;
            Q0 = qSketchRegion(id + "F12", true);
            extrude(context, id + "F13", {"entities" : qUnion([Q0]), "operationType" : NewBodyOperationType.ADD, "depth" : 25 * mm});
        }
        {
            var Q0;
            Q0=makeQuery(id+"F13.opExtrude","CAP_EDGE",EDGE,{"disambiguationData":[OSD([sQuery(id+"F12.wireOp",EDGE,"E22.right")])],"isStart":false});
            var Q1;
            Q1=makeQuery(id+"F13.opExtrude","CAP_EDGE",EDGE,{"disambiguationData":[OSD([sQuery(id+"F12.wireOp",EDGE,"E22.left")])],"isStart":false});
            var Q2;
            Q2=makeQuery(id+"F13.opExtrude","CAP_EDGE",EDGE,{"disambiguationData":[OSD([sQuery(id+"F12.wireOp",EDGE,"E24.right")])],"isStart":false});
            var Q3;
            Q3=makeQuery(id+"F13.opExtrude","CAP_EDGE",EDGE,{"disambiguationData":[OSD([sQuery(id+"F12.wireOp",EDGE,"E24.left")])],"isStart":false});
            fillet(context, id + "F14", {"entities" : qUnion([Q0, Q1, Q2, Q3]), "radius" : 12.5 * mm, "tangentPropagation" : true, "allowEdgeOverflow" : false});
        }
        {
            var Q0;
            Q0=makeQuery(id+"F13.opExtrude","SWEPT_FACE",FACE,{"disambiguationData":[OSD([sQuery(id+"F12.wireOp",EDGE,"E22.bottom")])]});
            var sketch = newSketch(context, id + "F15", { "sketchPlane" : qUnion([Q0])});
            skCircle(sketch, "E25", {"center": v(162.5, 282.5) * mm, "radius": 5 * mm});
            skSolve(sketch);
        }
        {
            var Q0;
            Q0=makeQuery(id+"F15.imprint","IMPRINT",FACE,{"disambiguationData":[TD([[makeQuery(id+"F15.imprint","IMPRINT",EDGE,{"derivedFrom":sQuery(id+"F15.wireOp",EDGE,"E25")}),1.0]])]});
            extrude(context, id + "F16", {"entities" : qUnion([Q0]), "operationType" : NewBodyOperationType.REMOVE, "oppositeDirection" : true, "depth" : 298.75 * mm});
        }
    });
